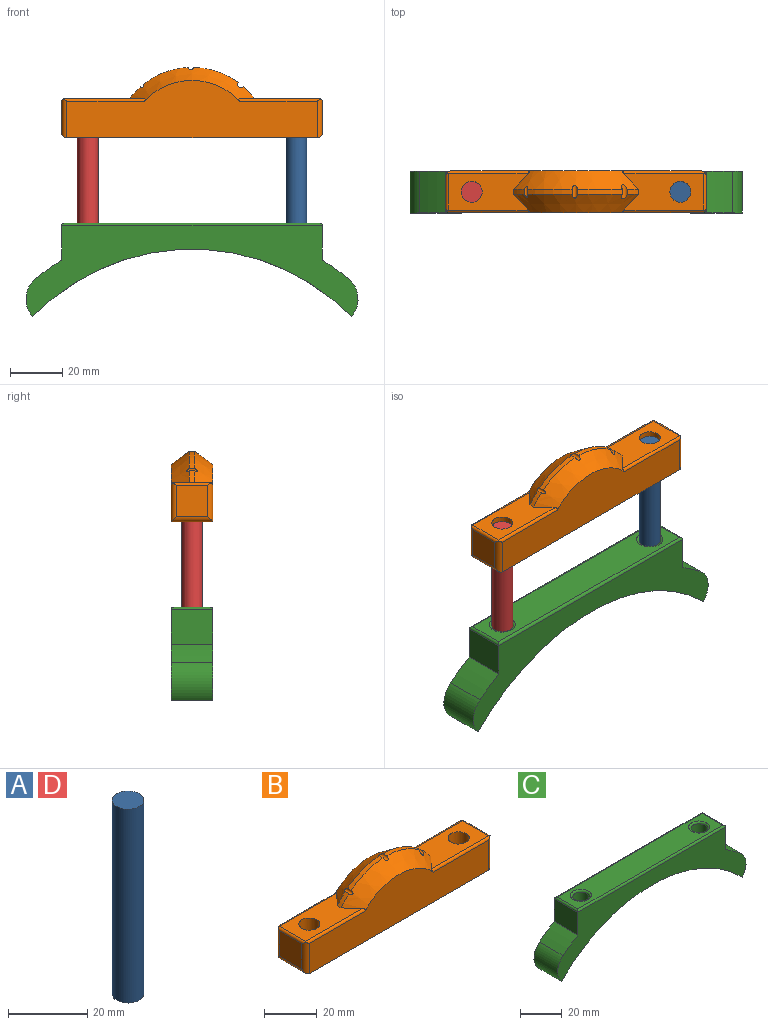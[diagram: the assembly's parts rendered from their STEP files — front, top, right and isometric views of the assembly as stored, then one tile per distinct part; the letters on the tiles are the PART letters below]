
ASSEMBLY  parts=4 mates=4
PART A: 3 faces, bbox 8x8x60 mm
  f0: cylinder r=4mm len=60mm, axis (0,0,-1), area 1508mm2, adj f1,f2
  f1: plane 8x8mm, normal (0,0,1), area 50.3mm2, adj f0
  f2: plane 8x8mm, normal (0,0,-1), area 50.3mm2, adj f0
PART B: 30 faces, bbox 100x16x27 mm
  f0: cylinder r=30mm len=4.52mm, axis (0,1,0), area 12.3mm2, adj f4,f11,f12,f14
  f1: cylinder r=30mm len=17.26mm, axis (0,1,0), area 37mm2, adj f11,f12,f13,f15
  f2: cylinder r=30mm len=4.62mm, axis (0,1,0), area 12.6mm2, adj f8,f11,f12,f13
  f3: cylinder r=30mm len=17.17mm, axis (0,1,0), area 37.3mm2, adj f11,f12,f14,f15
  f4: plane 30.64x14mm, normal (0,0,1), area 332.9mm2, adj f0,f11,f12,f17,f18,f19,f20
  f5: plane 12x12mm, normal (-1,0,0), area 144mm2, adj f20,f27,f28,f29
  f6: plane 96x16mm, normal (0,0,-1), area 1435.5mm2, adj f9,f10,f16,f17,f25,f29
  f7: plane 12x12mm, normal (1,0,0), area 144mm2, adj f23,f24,f25,f26
  f8: plane 30.64x14mm, normal (0,0,1), area 332.9mm2, adj f2,f11,f12,f16,f21,f22,f23
  f9: plane 96x22mm, normal (0,-1,0), area 1546.8mm2, adj f6,f12,f18,f21,f26,f27
  f10: plane 96x22mm, normal (0,1,0), area 1546.8mm2, adj f6,f11,f19,f22,f24,f28
  f11: cone r=30mm half-angle=35.5deg, axis (0,-1,0), area 397.5mm2, adj f0,f1,f2,f3,f4,f8,f10,f13
  f12: cone r=25mm half-angle=35.5deg, axis (0,1,0), area 397.5mm2, adj f0,f1,f2,f3,f4,f8,f9,f13
  f13: cylinder r=1.25mm len=5.5mm, axis (0,-1,0), area 16.4mm2, adj f1,f2,f11,f12
  f14: cylinder r=0.75mm len=4.1mm, axis (0,-1,0), area 7.8mm2, adj f0,f3,f11,f12
  f15: cylinder r=1mm len=4.8mm, axis (0,-1,0), area 11.7mm2, adj f1,f3,f11,f12
  f16: cylinder r=4mm len=15mm, axis (0,0,1), area 377mm2, adj f6,f8
  f17: cylinder r=4mm len=15mm, axis (0,0,1), area 377mm2, adj f4,f6
  f18: cylinder r=1mm len=31.47mm, axis (1,0,0), area 48.3mm2, adj f4,f9,f12,f20,f27
  f19: cylinder r=1mm len=31.47mm, axis (-1,0,0), area 48.3mm2, adj f4,f10,f11,f20,f28
  f20: cylinder r=1mm len=14.83mm, axis (0,1,0), area 21.5mm2, adj f4,f5,f18,f19,f27,f28
  f21: cylinder r=1mm len=31.47mm, axis (1,0,0), area 48.3mm2, adj f8,f9,f12,f23,f26
  f22: cylinder r=1mm len=31.47mm, axis (-1,0,0), area 48.3mm2, adj f8,f10,f11,f23,f24
  f23: cylinder r=1mm len=14.83mm, axis (0,1,0), area 21.5mm2, adj f7,f8,f21,f22,f24,f26
  f24: cylinder r=2mm len=14.91mm, axis (0,0,1), area 43.1mm2, adj f7,f10,f22,f23,f25
  f25: cylinder r=2mm len=16mm, axis (0,-1,0), area 45.7mm2, adj f6,f7,f24,f26
  f26: cylinder r=2mm len=14.91mm, axis (0,0,-1), area 43.1mm2, adj f7,f9,f21,f23,f25
  f27: cylinder r=2mm len=14.91mm, axis (0,0,1), area 43.1mm2, adj f5,f9,f18,f20,f29
  f28: cylinder r=2mm len=14.91mm, axis (0,0,-1), area 43.1mm2, adj f5,f10,f19,f20,f29
  f29: cylinder r=2mm len=16mm, axis (0,-1,0), area 45.7mm2, adj f5,f6,f27,f28
PART C: 18 faces, bbox 127.4x16x35.9 mm
  f0: plane 98x14mm, normal (0,0,1), area 1214.9mm2, adj f12,f13,f14,f15,f16,f17
  f1: cylinder r=85mm len=122.1mm, axis (0,1,0), area 2065mm2, adj f2,f7,f8,f9,f10,f11
  f2: cylinder r=10mm len=16mm, axis (0,1,0), area 260.7mm2, adj f1,f3,f8,f9
  f3: cylinder r=95mm len=16mm, axis (0,1,0), area 196.6mm2, adj f2,f4,f8,f9
  f4: plane 16x13.22mm, normal (1,0,0), area 211.6mm2, adj f3,f8,f9,f14
  f5: plane 16x13.22mm, normal (-1,0,0), area 211.6mm2, adj f6,f8,f9,f17
  f6: cylinder r=95mm len=16mm, axis (0,1,0), area 196.6mm2, adj f5,f7,f8,f9
  f7: cylinder r=10mm len=16mm, axis (0,1,0), area 260.7mm2, adj f1,f6,f8,f9
  f8: plane 127.37x34.86mm, normal (0,-1,0), area 1750.4mm2, adj f1,f2,f3,f4,f5,f6,f7,f15
  f9: plane 127.37x34.86mm, normal (0,1,0), area 1750.4mm2, adj f1,f2,f3,f4,f5,f6,f7,f16
  f10: cylinder r=4mm len=21.27mm, axis (0,0,1), area 479.2mm2, adj f1,f12
  f11: cylinder r=4mm len=21.28mm, axis (0,0,1), area 479.2mm2, adj f1,f13
  f12: torus R=5mm, axis (0,0,-1), area 43.1mm2, adj f0,f10
  f13: torus R=5mm, axis (0,0,-1), area 43.1mm2, adj f0,f11
  f14: cylinder r=1mm len=16mm, axis (0,-1,0), area 24mm2, adj f0,f4,f15,f16
  f15: cylinder r=1mm len=100mm, axis (1,0,0), area 155.9mm2, adj f0,f8,f14,f17
  f16: cylinder r=1mm len=100mm, axis (-1,0,0), area 155.9mm2, adj f0,f9,f14,f17
  f17: cylinder r=1mm len=16mm, axis (0,1,0), area 24mm2, adj f0,f5,f15,f16
PART D: same geometry as A
PLACE A t=(57.29,-78.7,55.18)mm
PLACE B t=(-199.67,-44.25,11.01)mm
PLACE C t=(-7.69,-44.25,-33.23)mm
PLACE D t=(-22.71,-78.7,55.18)mm
MATE cylindrical B.f17 <-> D.f0  axis (0,0,1) through (-189.67,-52.25,117.3)mm
MATE planar D.f0 <-> A.f0  axis (0,0,1) through (-189.67,-52.25,115.18)mm
MATE cylindrical A.f0 <-> C.f10  axis (0,0,-1) through (-109.67,-52.25,85.18)mm
MATE cylindrical D.f0 <-> C.f11  axis (0,0,-1) through (-189.67,-52.25,85.18)mm
